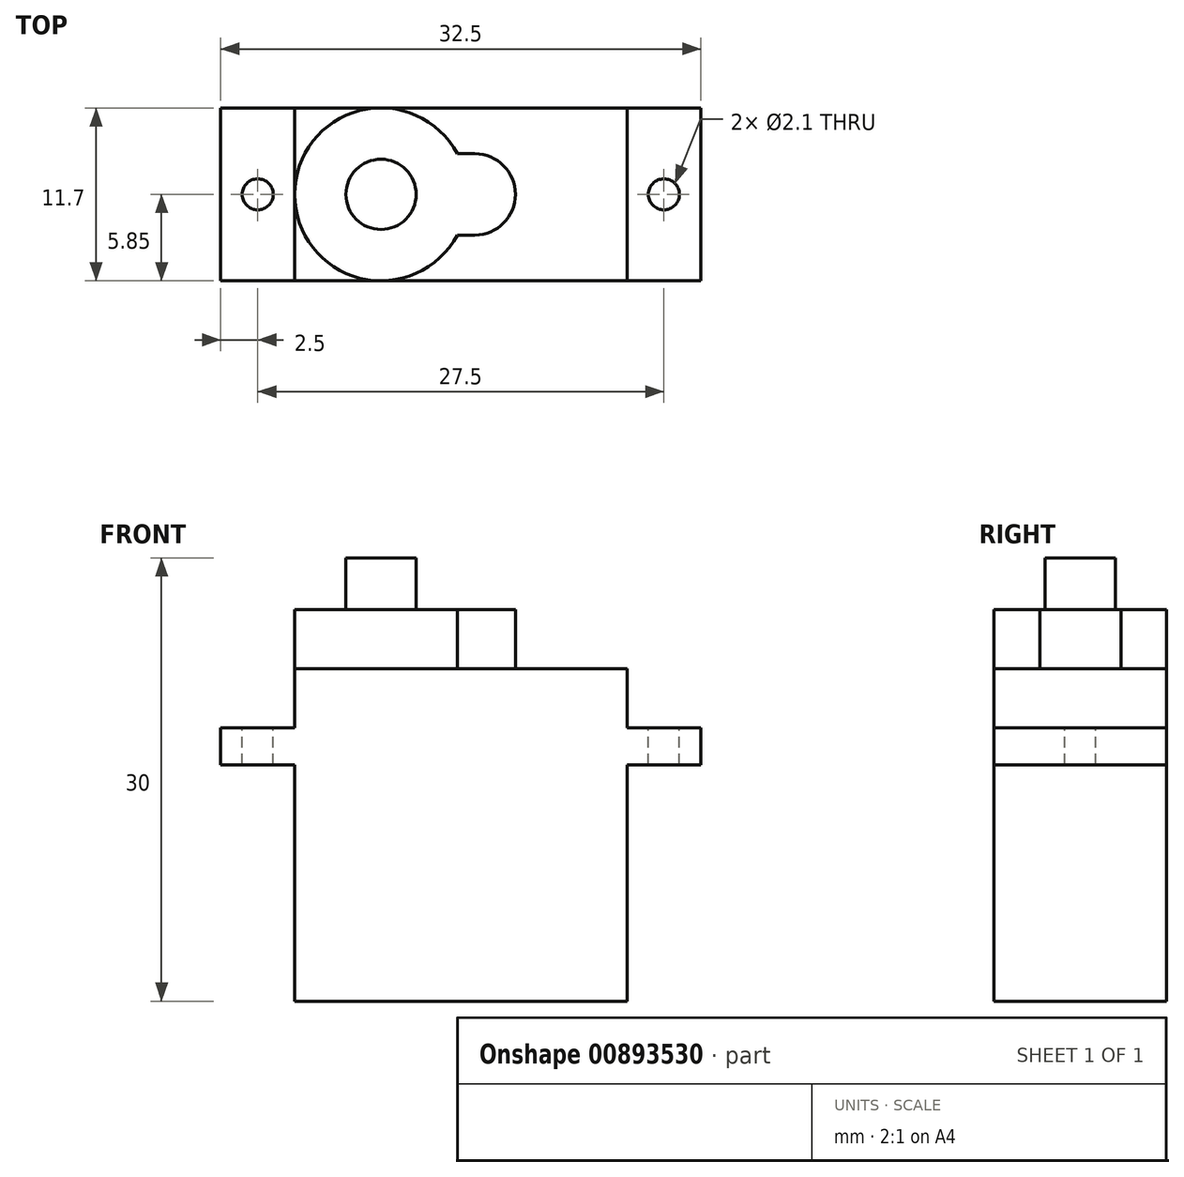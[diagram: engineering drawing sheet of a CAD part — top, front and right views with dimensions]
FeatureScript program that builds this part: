
annotation { "Feature Type Name" : "Feature", "Feature Type Description" : "" }
export const myFeature = defineFeature(function(context is Context, id is Id, definition is map)
    precondition{}
    {
        {
            var Q0;
            Q0=qCreatedBy(makeId("Front.planeOp"),FACE);
            var sketch = newSketch(context, id + "F0", { "sketchPlane" : qUnion([Q0])});
            skLineSegment(sketch, "E0.bottom", {"start": v(11.25, -11.25) * mm, "end": v(-11.25, -11.25) * mm});
            skLineSegment(sketch, "E0.top", {"start": v(11.25, 11.25) * mm, "end": v(-11.25, 11.25) * mm});
            skLineSegment(sketch, "E0.left", {"start": v(11.25, -11.25) * mm, "end": v(11.25, 11.25) * mm});
            skLineSegment(sketch, "E0.right", {"start": v(-11.25, -11.25) * mm, "end": v(-11.25, 11.25) * mm});
            skPoint(sketch, "E0.middle", {"position": v(0, 0) * mm});
            skLineSegment(sketch, "E1.bottom", {"start": v(16.25, 4.75) * mm, "end": v(-16.25, 4.75) * mm});
            skLineSegment(sketch, "E1.top", {"start": v(16.25, 7.25) * mm, "end": v(-16.25, 7.25) * mm});
            skLineSegment(sketch, "E1.left", {"start": v(16.25, 4.75) * mm, "end": v(16.25, 7.25) * mm});
            skLineSegment(sketch, "E1.right", {"start": v(-16.25, 4.75) * mm, "end": v(-16.25, 7.25) * mm});
            skPoint(sketch, "E1.middle", {"position": v(0, 6) * mm});
            skSolve(sketch);
        }
        {
            var Q0;
            Q0 = qSketchRegion(id + "F0", true);
            extrude(context, id + "F1", {"entities" : qUnion([Q0]), "depth" : 11.7 * mm, "offsetDistance" : 25 * mm});
        }
        {
            var Q0;
            Q0=makeQuery(id+"F1.opExtrude","SWEPT_FACE",FACE,{"disambiguationData":[OSD([sQuery(id+"F0.wireOp",EDGE,"E0.top")])]});
            var sketch = newSketch(context, id + "F2", { "sketchPlane" : qUnion([Q0])});
            skCircle(sketch, "E2", {"center": v(-5.4, -5.85) * mm, "radius": 5.85 * mm});
            skCircle(sketch, "E3", {"center": v(0.95, -5.85) * mm, "radius": 2.75 * mm});
            skLineSegment(sketch, "E4", {"start": v(0.95, -8.6) * mm, "end": v(-0.24, -8.6) * mm});
            skLineSegment(sketch, "E5", {"start": v(0.95, -3.1) * mm, "end": v(-0.24, -3.1) * mm});
            skLineSegment(sketch, "E6", {"start": v(0.95, -5.85) * mm, "end": v(-5.4, -5.85) * mm, "construction": true});
            skSolve(sketch);
        }
        {
            var Q0;
            Q0 = qSketchRegion(id + "F2", true);
            var Q1;
            {var subQ0=sQuery(id+"F2.wireOp",EDGE,"E3");var subQ1=sQuery(id+"F2.wireOp",EDGE,"E2");var subQ2=makeQuery(id+"F2.imprint","INTERSECT",VERTEX,{"disambiguationData":[OD(0.0)],"derivedFrom":[subQ1,subQ0]});Q1=makeQuery(id+"F2.imprint","IMPRINT",FACE,{"disambiguationData":[TD([[makeQuery(id+"F2.imprint","IMPRINT",EDGE,{"disambiguationData":[TD([[subQ2,1.0]])],"derivedFrom":subQ1}),1.0]])]});}
            extrude(context, id + "F3", {"entities" : qUnion([Q0, Q1]), "operationType" : NewBodyOperationType.ADD, "depth" : 4 * mm, "offsetDistance" : 25 * mm});
        }
        {
            var Q0;
            {var subQ0=sQuery(id+"F0.wireOp",EDGE,"E1.top");Q0=makeQuery(id+"F1.opExtrude","SWEPT_FACE",FACE,{"disambiguationData":[OSD([subQ0]),TDD([makeQuery(id+"F0.imprint","IMPRINT",EDGE,{"disambiguationData":[TD([[makeQuery(id+"F0.imprint","INTERSECT",VERTEX,{"derivedFrom":[subQ0,sQuery(id+"F0.wireOp",EDGE,"E1.right")]}),1.0]])],"derivedFrom":subQ0})])]});}
            var sketch = newSketch(context, id + "F4", { "sketchPlane" : qUnion([Q0])});
            skCircle(sketch, "E7", {"center": v(-13.75, -5.85) * mm, "radius": 1.05 * mm});
            skCircle(sketch, "E8", {"center": v(13.75, -5.85) * mm, "radius": 1.05 * mm});
            skLineSegment(sketch, "E9", {"start": v(13.75, -5.85) * mm, "end": v(16.25, -5.85) * mm, "construction": true});
            skLineSegment(sketch, "E10", {"start": v(-13.75, -5.85) * mm, "end": v(-16.25, -5.85) * mm, "construction": true});
            skLineSegment(sketch, "E11", {"start": v(13.75, -5.85) * mm, "end": v(11.25, -5.85) * mm, "construction": true});
            skLineSegment(sketch, "E12", {"start": v(-13.75, -5.85) * mm, "end": v(-11.25, -5.85) * mm, "construction": true});
            skSolve(sketch);
        }
        {
            var Q0;
            Q0 = qSketchRegion(id + "F4", true);
            extrude(context, id + "F5", {"entities" : qUnion([Q0]), "operationType" : NewBodyOperationType.REMOVE, "oppositeDirection" : true, "depth" : 25 * mm, "offsetDistance" : 25 * mm});
        }
        {
            var Q0;
            Q0=makeQuery(id+"F3.opExtrude","CAP_FACE",FACE,{"disambiguationData":[OSD([sQuery(id+"F2.wireOp",EDGE,"E2"),sQuery(id+"F2.wireOp",EDGE,"E3"),sQuery(id+"F2.wireOp",EDGE,"E4"),sQuery(id+"F2.wireOp",EDGE,"E5")])],"isStart":false});
            var sketch = newSketch(context, id + "F6", { "sketchPlane" : qUnion([Q0])});
            skCircle(sketch, "E13", {"center": v(-5.4, -5.85) * mm, "radius": 2.38 * mm});
            skSolve(sketch);
        }
        {
            var Q0;
            Q0 = qSketchRegion(id + "F6", true);
            extrude(context, id + "F7", {"entities" : qUnion([Q0]), "operationType" : NewBodyOperationType.ADD, "depth" : 3.5 * mm, "offsetDistance" : 25 * mm});
        }
    });
